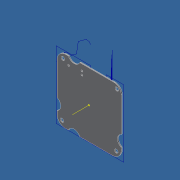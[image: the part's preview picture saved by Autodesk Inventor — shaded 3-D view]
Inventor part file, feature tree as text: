
AUTODESK INVENTOR PART (.ipt)
format: ipt  version: 2016 (Build 200138000, 138)  size: 2,686,464 bytes
history: native  units: in
note: dims shown in document units (in); Inventor stores cm internally (conversion verified against a paired STEP export)
features: other x6, extrude x1
ambient origin geometry x8: Origin, YZ Plane, XZ Plane, XY Plane, X Axis, Y Axis, Z Axis, Center Point
bodies: Solid1 (feature_tree)
feature tree (7):
  extrude  "Extrusion1"  Depth=0.024in TaperAngle=0.0deg
  other  "Work Point1"
  other  "Work Axis1"
  other  "Work Point2"
  other  "Work Point3"
  other  "Work Axis2"
  other  "Work Axis3"
